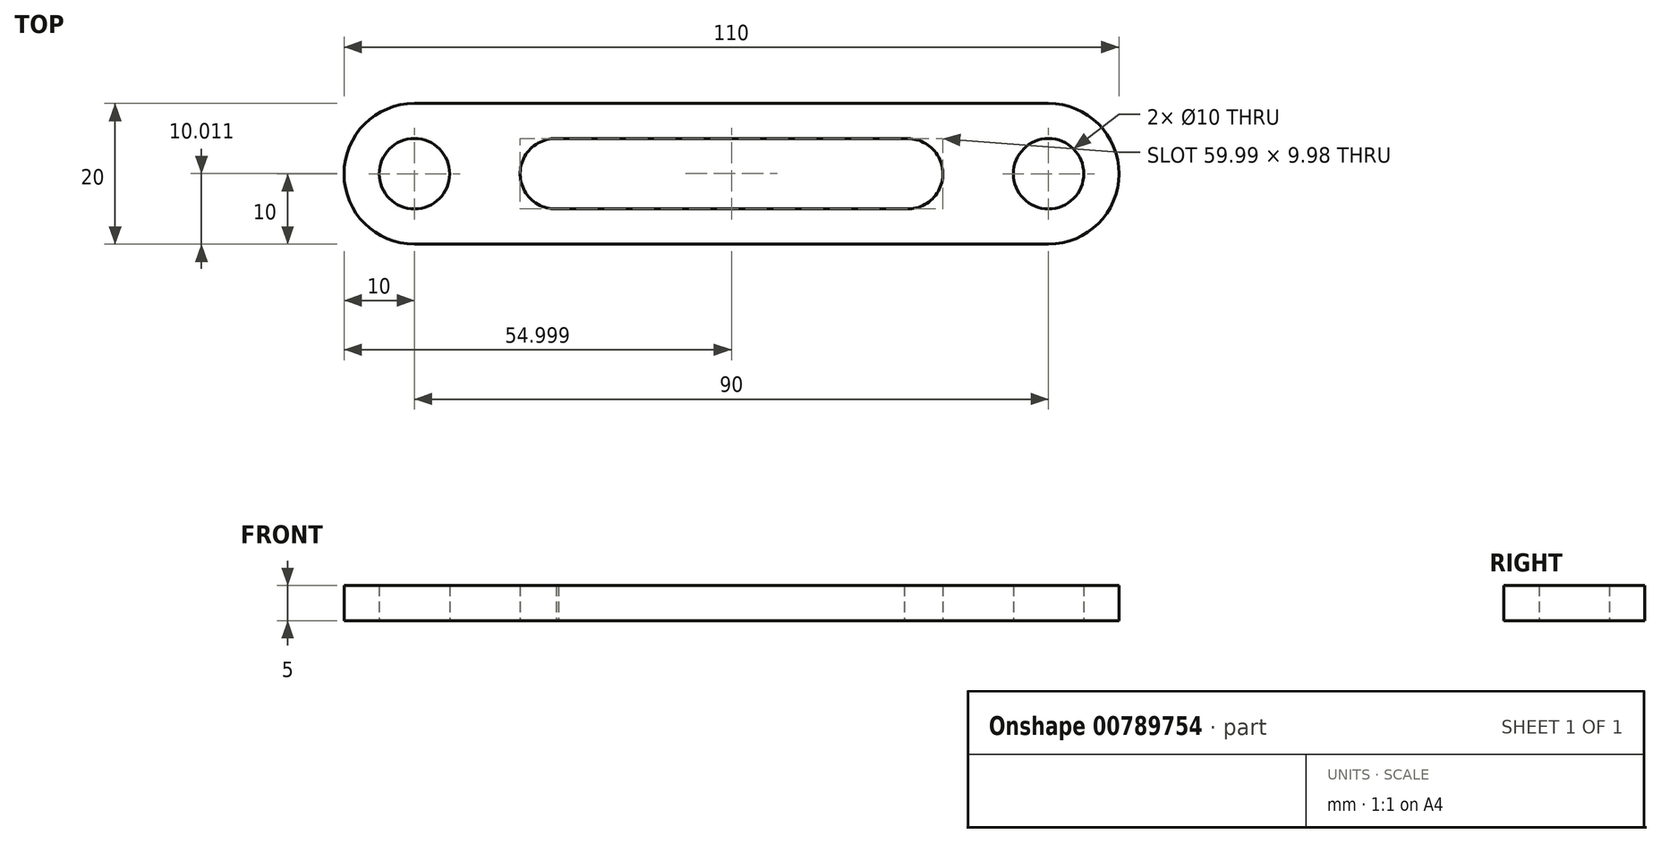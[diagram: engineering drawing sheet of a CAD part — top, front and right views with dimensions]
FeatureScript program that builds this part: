
annotation { "Feature Type Name" : "Feature", "Feature Type Description" : "" }
export const myFeature = defineFeature(function(context is Context, id is Id, definition is map)
    precondition{}
    {
        {
            var Q0;
            Q0=qCreatedBy(makeId("Top.planeOp"),FACE);
            var sketch = newSketch(context, id + "F0", { "sketchPlane" : qUnion([Q0])});
            skArc(sketch, "E0", {"start": v(0, 10) * mm, "mid": v(-10, 0) * mm, "end": v(0, -10) * mm});
            skArc(sketch, "E1", {"start": v(90, -10) * mm, "mid": v(100, 0) * mm, "end": v(90, 10) * mm});
            skLineSegment(sketch, "E2", {"start": v(0, -10) * mm, "end": v(90, -10) * mm});
            skLineSegment(sketch, "E3", {"start": v(0, 10) * mm, "end": v(90, 10) * mm});
            skCircle(sketch, "E4", {"center": v(0, 0) * mm, "radius": 5 * mm});
            skCircle(sketch, "E5", {"center": v(90, 0) * mm, "radius": 5 * mm});
            skArc(sketch, "E6", {"start": v(20.14, 5) * mm, "mid": v(15, -0.16) * mm, "end": v(20.47, -4.98) * mm});
            skArc(sketch, "E7", {"start": v(69.53, -4.98) * mm, "mid": v(75, -0.23) * mm, "end": v(70, 5) * mm});
            skLineSegment(sketch, "E8", {"start": v(20.14, 5) * mm, "end": v(70, 5) * mm});
            skLineSegment(sketch, "E9", {"start": v(20.47, -4.98) * mm, "end": v(70.47, -4.98) * mm});
            skSolve(sketch);
        }
        {
            var Q0;
            Q0=makeQuery(id+"F0.imprint","IMPRINT",FACE,{"disambiguationData":[TD([[makeQuery(id+"F0.imprint","IMPRINT",EDGE,{"derivedFrom":sQuery(id+"F0.wireOp",EDGE,"E0")}),1.0]])]});
            extrude(context, id + "F1", {"entities" : qUnion([Q0]), "depth" : 5 * mm, "offsetDistance" : 25 * mm});
        }
    });
